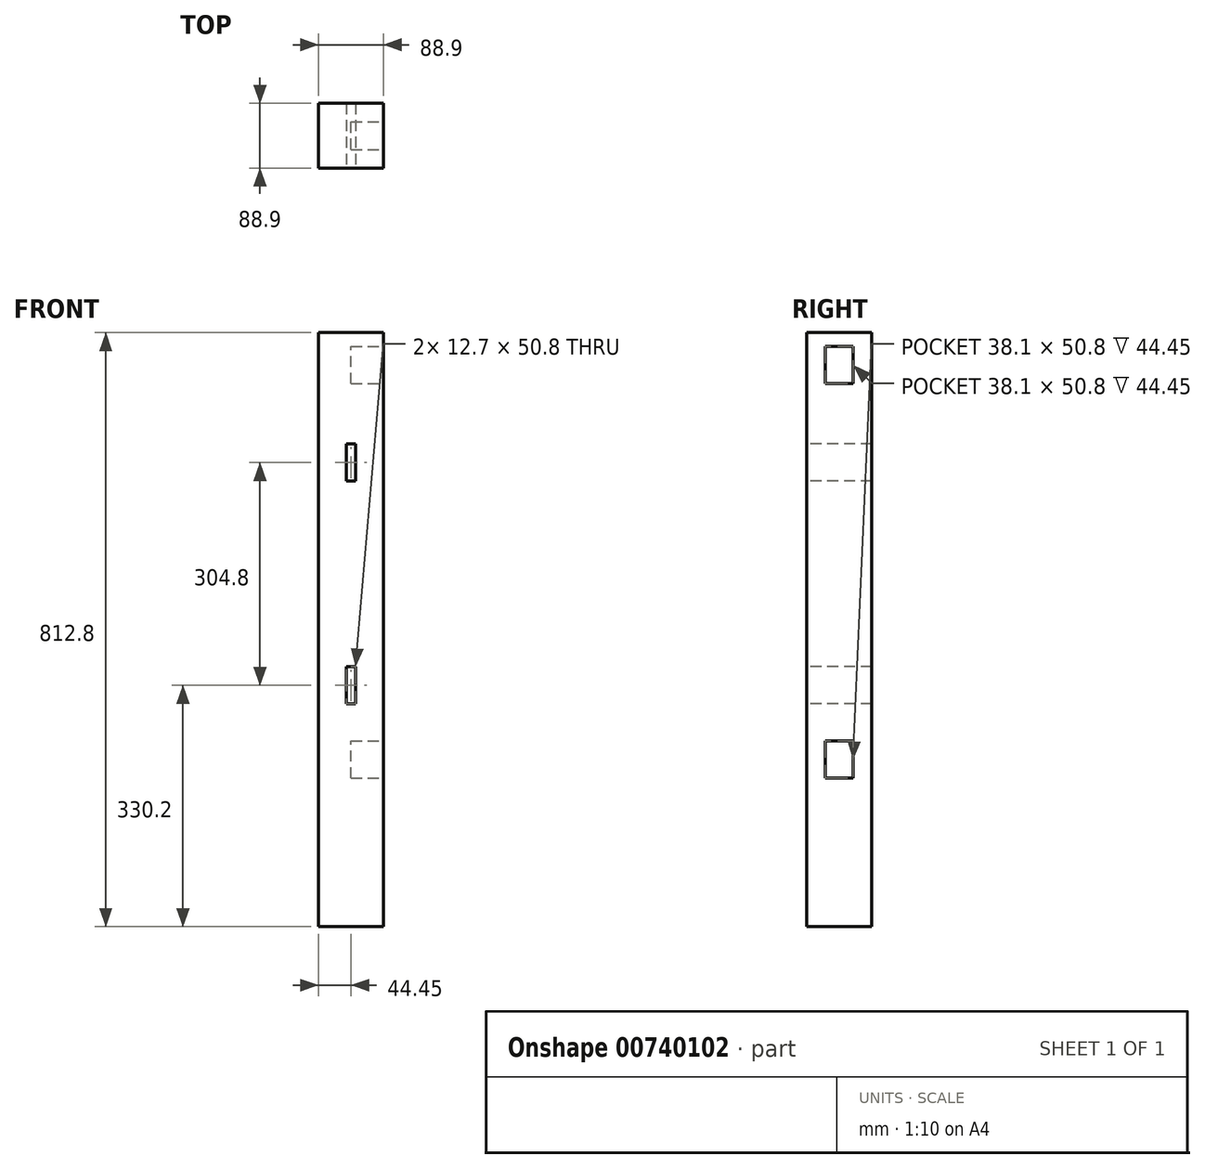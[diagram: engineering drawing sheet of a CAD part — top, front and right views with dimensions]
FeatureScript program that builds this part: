
annotation { "Feature Type Name" : "Feature", "Feature Type Description" : "" }
export const myFeature = defineFeature(function(context is Context, id is Id, definition is map)
    precondition{}
    {
        {
            var Q0;
            Q0=qCreatedBy(makeId("Top.planeOp"),FACE);
            var sketch = newSketch(context, id + "F0", { "sketchPlane" : qUnion([Q0])});
            skLineSegment(sketch, "E0.bottom", {"start": v(-44.45, 44.45) * mm, "end": v(44.45, 44.45) * mm});
            skLineSegment(sketch, "E0.top", {"start": v(-44.45, -44.45) * mm, "end": v(44.45, -44.45) * mm});
            skLineSegment(sketch, "E0.left", {"start": v(-44.45, 44.45) * mm, "end": v(-44.45, -44.45) * mm});
            skLineSegment(sketch, "E0.right", {"start": v(44.45, 44.45) * mm, "end": v(44.45, -44.45) * mm});
            skPoint(sketch, "E0.middle", {"position": v(0, 0) * mm});
            skSolve(sketch);
        }
        {
            var Q0;
            Q0 = qSketchRegion(id + "F0", true);
            extrude(context, id + "F1", {"entities" : qUnion([Q0]), "depth" : 812.8 * mm, "offsetDistance" : 25.4 * mm});
        }
        {
            var Q0;
            Q0=makeQuery(id+"F1.opExtrude","SWEPT_FACE",FACE,{"disambiguationData":[OSD([sQuery(id+"F0.wireOp",EDGE,"E0.right")])]});
            var sketch = newSketch(context, id + "F2", { "sketchPlane" : qUnion([Q0])});
            skLineSegment(sketch, "E1.bottom", {"start": v(-19.05, 742.95) * mm, "end": v(19.05, 742.95) * mm});
            skLineSegment(sketch, "E1.top", {"start": v(-19.05, 793.75) * mm, "end": v(19.05, 793.75) * mm});
            skLineSegment(sketch, "E1.left", {"start": v(-19.05, 742.95) * mm, "end": v(-19.05, 793.75) * mm});
            skLineSegment(sketch, "E1.right", {"start": v(19.05, 742.95) * mm, "end": v(19.05, 793.75) * mm});
            skPoint(sketch, "E1.middle", {"position": v(0, 768.35) * mm});
            skLineSegment(sketch, "E2.bottom", {"start": v(-19.05, 203.2) * mm, "end": v(19.05, 203.2) * mm});
            skLineSegment(sketch, "E2.top", {"start": v(-19.05, 254) * mm, "end": v(19.05, 254) * mm});
            skLineSegment(sketch, "E2.left", {"start": v(-19.05, 203.2) * mm, "end": v(-19.05, 254) * mm});
            skLineSegment(sketch, "E2.right", {"start": v(19.05, 203.2) * mm, "end": v(19.05, 254) * mm});
            skPoint(sketch, "E2.middle", {"position": v(0, 228.6) * mm});
            skSolve(sketch);
        }
        {
            var Q0;
            Q0 = qSketchRegion(id + "F2", true);
            extrude(context, id + "F3", {"entities" : qUnion([Q0]), "operationType" : NewBodyOperationType.REMOVE, "oppositeDirection" : true, "depth" : 44.45 * mm, "offsetDistance" : 25.4 * mm});
        }
        {
            var Q0;
            Q0=makeQuery(id+"F1.opExtrude","SWEPT_FACE",FACE,{"disambiguationData":[OSD([sQuery(id+"F0.wireOp",EDGE,"E0.top")])]});
            var sketch = newSketch(context, id + "F4", { "sketchPlane" : qUnion([Q0])});
            skLineSegment(sketch, "E3", {"start": v(0, 812.8) * mm, "end": v(0, 0) * mm, "construction": true});
            skLineSegment(sketch, "E4.bottom", {"start": v(-6.35, 660.4) * mm, "end": v(6.35, 660.4) * mm});
            skLineSegment(sketch, "E4.top", {"start": v(-6.35, 609.6) * mm, "end": v(6.35, 609.6) * mm});
            skLineSegment(sketch, "E4.left", {"start": v(-6.35, 660.4) * mm, "end": v(-6.35, 609.6) * mm});
            skLineSegment(sketch, "E4.right", {"start": v(6.35, 660.4) * mm, "end": v(6.35, 609.6) * mm});
            skPoint(sketch, "E4.middle", {"position": v(0, 635) * mm});
            skLineSegment(sketch, "E5", {"start": v(-44.45, 406.4) * mm, "end": v(44.45, 406.4) * mm, "construction": true});
            skLineSegment(sketch, "E6.bottom", {"start": v(-6.35, 355.6) * mm, "end": v(6.35, 355.6) * mm});
            skLineSegment(sketch, "E6.top", {"start": v(-6.35, 304.8) * mm, "end": v(6.35, 304.8) * mm});
            skLineSegment(sketch, "E6.left", {"start": v(-6.35, 355.6) * mm, "end": v(-6.35, 304.8) * mm});
            skLineSegment(sketch, "E6.right", {"start": v(6.35, 355.6) * mm, "end": v(6.35, 304.8) * mm});
            skPoint(sketch, "E6.middle", {"position": v(0, 330.2) * mm});
            skSolve(sketch);
        }
        {
            var Q0;
            Q0 = qSketchRegion(id + "F4", true);
            extrude(context, id + "F5", {"entities" : qUnion([Q0]), "operationType" : NewBodyOperationType.REMOVE, "endBound" : BoundingType.THROUGH_ALL, "oppositeDirection" : true, "depth" : 25.4 * mm, "offsetDistance" : 25.4 * mm});
        }
    });
